# Revit family: 1359xxx Avlon 1200 UL Phase
name_source: partatom
category: Lighting Fixtures
units: mm (PartAtom-declared; Revit-internal decimal feet)

## family parameters
Always vertical = Yes
Cut with Voids When Loaded = No
Host = Wall
Light Source = No
Maintain Annotation Orientation = No
OmniClass Number = 23.80.70.00
OmniClass Title = Lighting
Part Type = Normal
Room Calculation Point = No
Round Connector Dimension = Use Diameter
Shared = No

## types (2) — shared parameters
ADA compliant = Yes
Apparent Load = 0 VA
Dimmable = Yes
Dimming Method = Phase
Driver Included = Yes
Driver Required = No
Efficacy (lm/w) = To be advised
Electrical Class = 1
Lamp = LED
Length of Cable Supplied = Not applicable
Light Source Fixed = Yes
Location / IP Rating = Damp
Main Finish = Mirror Finish
Main Material = Glass - Float
Manufacturer = Astro Lighting Ltd
Manufacturer URL - Europe and Rest of World = www.astrolighting.com
Manufacturer URL - North America = us.astrolighting.com
Power (Watts) = 21.1
Product CRI = 90
Product Dimensions (MM) = 600x1200x36
Product Location = Bathroom
Product URL = https://us.astrolighting.com
Product Weight (KG) = 13.21
URL = www.astrolighting.com
zero-valued in all types: Default Elevation

## per-type parameters (varying)
| type | Product CCT | Product Name | Product SKU |
| Astro Avlon 1200 2700K Phase | 2700K | Avlon 1200 2700K Phase | 1359034 |
| Astro Avlon 1200 3000K Phase | 3000K | Avlon 1200 3000K Phase | 1359036 |

## geometry (parser evidence)
native form markers: Sweep x3
no freeform markers — native parametric forms only
